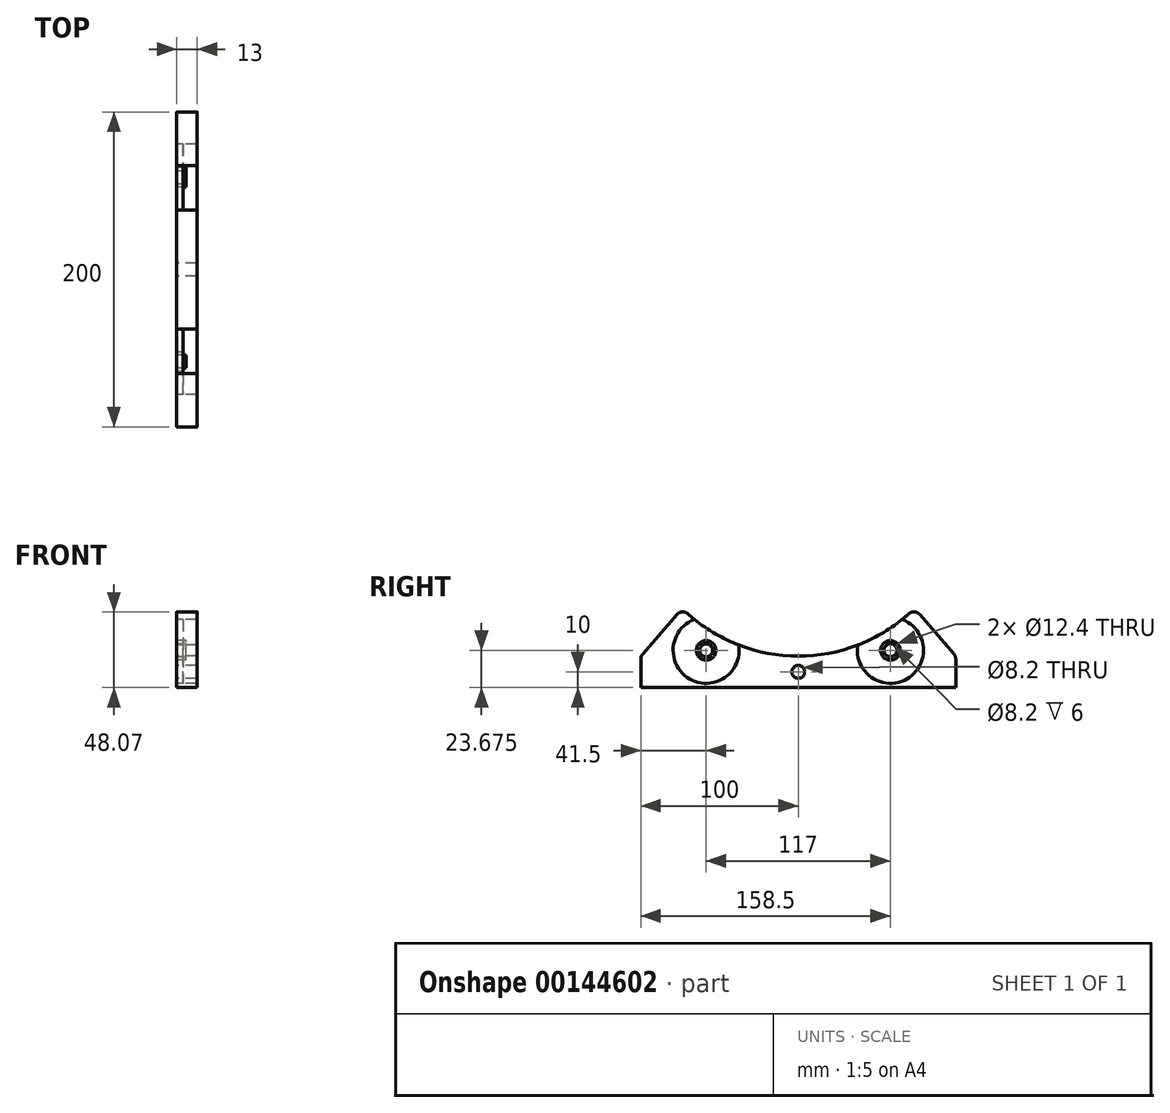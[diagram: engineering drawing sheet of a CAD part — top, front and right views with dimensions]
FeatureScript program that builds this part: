
annotation { "Feature Type Name" : "Feature", "Feature Type Description" : "" }
export const myFeature = defineFeature(function(context is Context, id is Id, definition is map)
    precondition{}
    {
        {
            var Q0;
            Q0=qCreatedBy(makeId("Right.planeOp"),FACE);
            var sketch = newSketch(context, id + "F0", { "sketchPlane" : qUnion([Q0])});
            skCircle(sketch, "E0", {"center": v(0, 0) * mm, "radius": 100 * mm});
            skLineSegment(sketch, "E1", {"start": v(0, 0) * mm, "end": v(0, -182.24) * mm, "construction": true});
            skLineSegment(sketch, "E2", {"start": v(0, 0) * mm, "end": v(96.48, -167.1) * mm, "construction": true});
            skLineSegment(sketch, "E3", {"start": v(50, -86.6) * mm, "end": v(58.5, -101.32) * mm, "construction": true});
            skCircle(sketch, "E4", {"center": v(58.5, -101.32) * mm, "radius": 4.1 * mm});
            skLineSegment(sketch, "E5", {"start": v(0, -105) * mm, "end": v(0, -125) * mm, "construction": true});
            skLineSegment(sketch, "E6", {"start": v(0, -125) * mm, "end": v(100, -125) * mm});
            skLineSegment(sketch, "E7", {"start": v(100, -125) * mm, "end": v(100, -106.86) * mm});
            skLineSegment(sketch, "E8", {"start": v(98.78, -103.6) * mm, "end": v(77.18, -78.66) * mm});
            skPoint(sketch, "E9.visualSharp", {"position": v(100, -105) * mm});
            skArc(sketch, "E9.filletArc", {"start": v(100, -106.86) * mm, "mid": v(99.68, -105.12) * mm, "end": v(98.78, -103.6) * mm});
            skArc(sketch, "E10", {"start": v(0, -105) * mm, "mid": v(37.5, -98.07) * mm, "end": v(70.06, -78.2) * mm});
            skPoint(sketch, "E11.visualSharp", {"position": v(73.77, -74.72) * mm});
            skArc(sketch, "E11.filletArc", {"start": v(77.18, -78.66) * mm, "mid": v(73.72, -76.94) * mm, "end": v(70.06, -78.2) * mm});
            skArc(sketch, "E12.MirrorCS", {"start": v(0, -105) * mm, "mid": v(-37.5, -98.07) * mm, "end": v(-70.06, -78.2) * mm});
            skArc(sketch, "E13.MirrorCS", {"start": v(-77.18, -78.66) * mm, "mid": v(-73.72, -76.94) * mm, "end": v(-70.06, -78.2) * mm});
            skLineSegment(sketch, "E14.MirrorCS", {"start": v(-98.78, -103.6) * mm, "end": v(-77.18, -78.66) * mm});
            skArc(sketch, "E15.MirrorCS", {"start": v(-100, -106.86) * mm, "mid": v(-99.68, -105.12) * mm, "end": v(-98.78, -103.6) * mm});
            skLineSegment(sketch, "E16.MirrorCS", {"start": v(-100, -125) * mm, "end": v(-100, -106.86) * mm});
            skLineSegment(sketch, "E17.MirrorCS", {"start": v(0, -125) * mm, "end": v(-100, -125) * mm});
            skPoint(sketch, "E18", {"position": v(0, -115) * mm});
            skCircle(sketch, "E19", {"center": v(0, -115) * mm, "radius": 4.1 * mm});
            skCircle(sketch, "E20.MirrorC", {"center": v(-58.5, -101.32) * mm, "radius": 4.1 * mm});
            skCircle(sketch, "E21", {"center": v(-58.5, -101.32) * mm, "radius": 6.2 * mm});
            skCircle(sketch, "E22", {"center": v(58.5, -101.32) * mm, "radius": 6.2 * mm});
            skCircle(sketch, "E23", {"center": v(-58.5, -101.32) * mm, "radius": 21 * mm});
            skCircle(sketch, "E24.MirrorC", {"center": v(58.5, -101.32) * mm, "radius": 21 * mm});
            skSolve(sketch);
        }
        {
            var Q0;
            Q0=makeQuery(id+"F0.imprint","IMPRINT",FACE,{"disambiguationData":[TD([[makeQuery(id+"F0.imprint","IMPRINT",EDGE,{"derivedFrom":sQuery(id+"F0.wireOp",EDGE,"E4")}),-1.0]])]});
            var Q1;
            Q1=makeQuery(id+"F0.imprint","IMPRINT",FACE,{"disambiguationData":[TD([[makeQuery(id+"F0.imprint","IMPRINT",EDGE,{"derivedFrom":sQuery(id+"F0.wireOp",EDGE,"E20.MirrorC")}),1.0]])]});
            extrude(context, id + "F1", {"entities" : qUnion([Q0, Q1]), "depth" : 6 * mm});
        }
        {
            var Q0;
            Q0=makeQuery(id+"F0.imprint","IMPRINT",FACE,{"disambiguationData":[TD([[makeQuery(id+"F0.imprint","IMPRINT",EDGE,{"derivedFrom":sQuery(id+"F0.wireOp",EDGE,"E21")}),-1.0]])]});
            var Q1;
            Q1=makeQuery(id+"F0.imprint","IMPRINT",FACE,{"disambiguationData":[TD([[makeQuery(id+"F0.imprint","IMPRINT",EDGE,{"derivedFrom":sQuery(id+"F0.wireOp",EDGE,"E22")}),-1.0]])]});
            extrude(context, id + "F2", {"entities" : qUnion([Q0, Q1]), "depth" : 4 * mm});
        }
        {
            var Q0;
            Q0=makeQuery(id+"F0.imprint","IMPRINT",FACE,{"disambiguationData":[TD([[makeQuery(id+"F0.imprint","IMPRINT",EDGE,{"derivedFrom":sQuery(id+"F0.wireOp",EDGE,"E6")}),1.0]])]});
            extrude(context, id + "F3", {"entities" : qUnion([Q0]), "depth" : 13 * mm});
        }
    });
